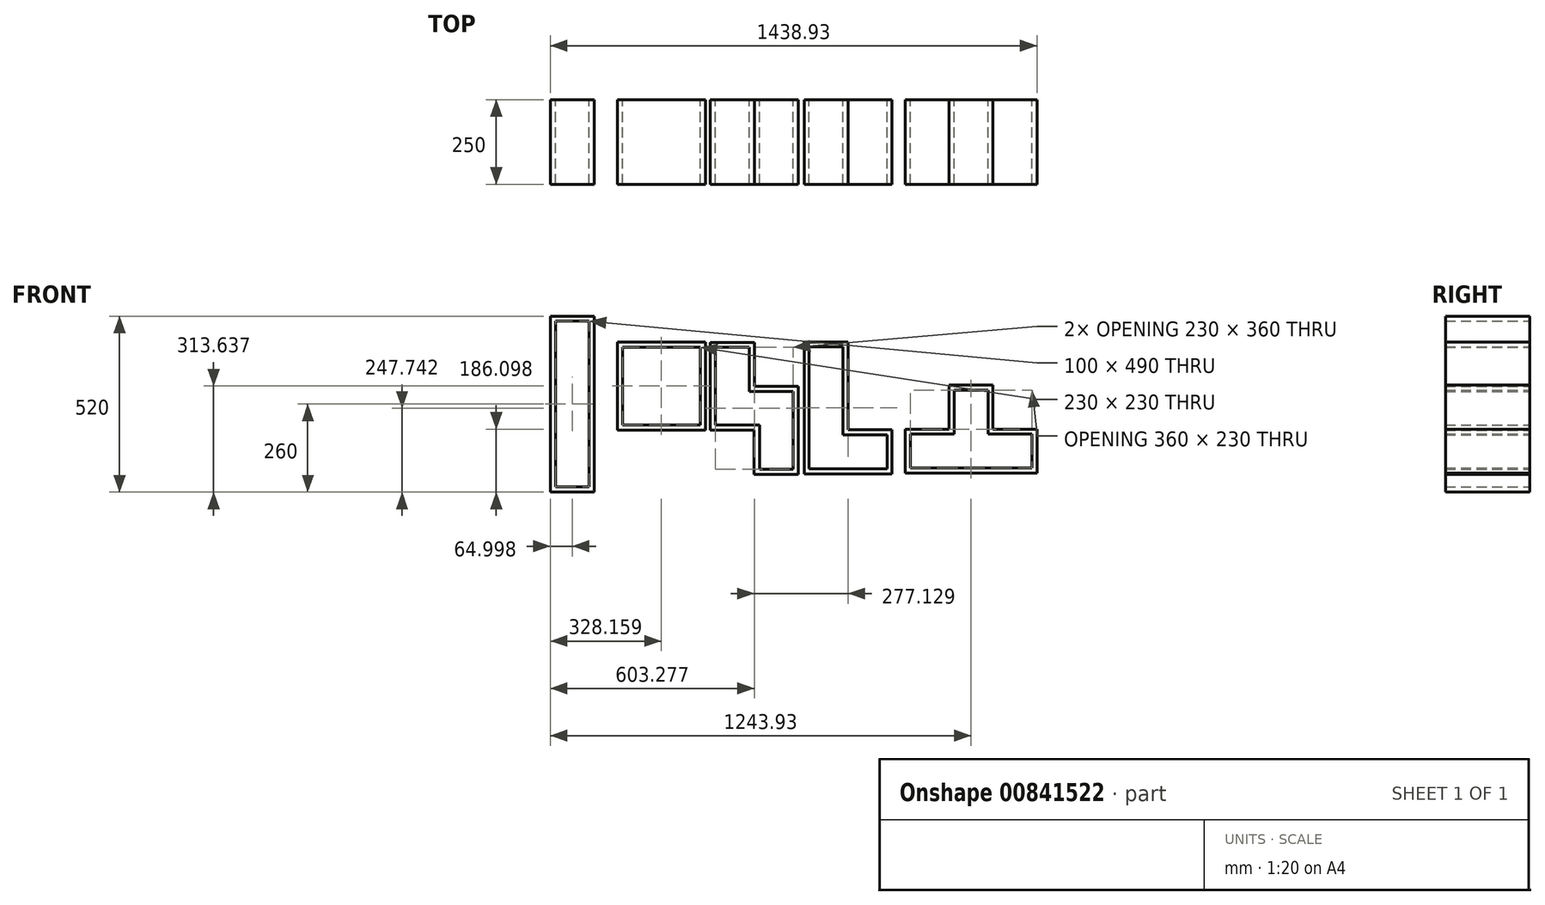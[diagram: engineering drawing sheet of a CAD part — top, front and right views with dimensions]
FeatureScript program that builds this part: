
annotation { "Feature Type Name" : "Feature", "Feature Type Description" : "" }
export const myFeature = defineFeature(function(context is Context, id is Id, definition is map)
    precondition{}
    {
        {
            var Q0;
            Q0=qCreatedBy(makeId("Front.planeOp"),FACE);
            var sketch = newSketch(context, id + "F0", { "sketchPlane" : qUnion([Q0])});
            skLineSegment(sketch, "E0", {"start": v(-196, 207.37) * mm, "end": v(-66, 207.37) * mm});
            skLineSegment(sketch, "E1", {"start": v(-66, 207.37) * mm, "end": v(-66, 77.37) * mm});
            skLineSegment(sketch, "E2", {"start": v(-66, 77.37) * mm, "end": v(64, 77.37) * mm});
            skLineSegment(sketch, "E3", {"start": v(64, 77.37) * mm, "end": v(64, -182.63) * mm});
            skLineSegment(sketch, "E4", {"start": v(64, -182.63) * mm, "end": v(-67, -182.63) * mm});
            skLineSegment(sketch, "E5", {"start": v(-67, -182.63) * mm, "end": v(-67, -52.63) * mm});
            skLineSegment(sketch, "E6", {"start": v(-196, -52.63) * mm, "end": v(-196, 207.37) * mm});
            skLineSegment(sketch, "E7", {"start": v(-196, -52.63) * mm, "end": v(-67, -52.63) * mm});
            skLineSegment(sketch, "E8", {"start": v(-181, 192.37) * mm, "end": v(-181, -37.63) * mm});
            skLineSegment(sketch, "E9", {"start": v(-181, -37.63) * mm, "end": v(-51, -37.63) * mm});
            skLineSegment(sketch, "E10", {"start": v(-51, -37.63) * mm, "end": v(-51, -167.63) * mm});
            skLineSegment(sketch, "E11", {"start": v(-51, -167.63) * mm, "end": v(49, -167.63) * mm});
            skLineSegment(sketch, "E12", {"start": v(49, -167.63) * mm, "end": v(49, 62.37) * mm});
            skLineSegment(sketch, "E13", {"start": v(49, 62.37) * mm, "end": v(-81, 62.37) * mm});
            skLineSegment(sketch, "E14", {"start": v(-81, 62.37) * mm, "end": v(-81, 192.37) * mm});
            skLineSegment(sketch, "E15", {"start": v(-81, 192.37) * mm, "end": v(-181, 192.37) * mm});
            skLineSegment(sketch, "E16", {"start": v(-196, 175.02) * mm, "end": v(-181, 175.02) * mm, "construction": true});
            skLineSegment(sketch, "E17", {"start": v(-131, 207.37) * mm, "end": v(-131, 192.37) * mm, "construction": true});
            skLineSegment(sketch, "E18", {"start": v(-3.9, 77.37) * mm, "end": v(-3.9, 62.37) * mm, "construction": true});
            skLineSegment(sketch, "E19", {"start": v(49, -86.83) * mm, "end": v(64, -86.83) * mm, "construction": true});
            skLineSegment(sketch, "E20", {"start": v(10.57, -167.63) * mm, "end": v(10.57, -182.63) * mm, "construction": true});
            skLineSegment(sketch, "E21", {"start": v(-144.39, -37.63) * mm, "end": v(-144.39, -52.63) * mm, "construction": true});
            skSolve(sketch);
        }
        {
            var Q0;
            Q0=qCreatedBy(makeId("Front.planeOp"),FACE);
            var sketch = newSketch(context, id + "F1", { "sketchPlane" : qUnion([Q0])});
            skLineSegment(sketch, "E22.bottom", {"start": v(-471.11, 208.27) * mm, "end": v(-211.11, 208.27) * mm});
            skLineSegment(sketch, "E22.top", {"start": v(-471.11, -51.73) * mm, "end": v(-211.11, -51.73) * mm});
            skLineSegment(sketch, "E22.left", {"start": v(-471.11, 208.27) * mm, "end": v(-471.11, -51.73) * mm});
            skLineSegment(sketch, "E22.right", {"start": v(-211.11, 208.27) * mm, "end": v(-211.11, -51.73) * mm});
            skLineSegment(sketch, "E23.bottom", {"start": v(-456.11, 193.27) * mm, "end": v(-226.11, 193.27) * mm});
            skLineSegment(sketch, "E23.top", {"start": v(-456.11, -36.73) * mm, "end": v(-226.11, -36.73) * mm});
            skLineSegment(sketch, "E23.left", {"start": v(-456.11, 193.27) * mm, "end": v(-456.11, -36.73) * mm});
            skLineSegment(sketch, "E23.right", {"start": v(-226.11, 193.27) * mm, "end": v(-226.11, -36.73) * mm});
            skLineSegment(sketch, "E24", {"start": v(-471.11, 102.95) * mm, "end": v(-456.11, 102.95) * mm, "construction": true});
            skLineSegment(sketch, "E25", {"start": v(-393.58, -36.73) * mm, "end": v(-393.58, -51.73) * mm, "construction": true});
            skSolve(sketch);
        }
        {
            var Q0;
            Q0=qCreatedBy(makeId("Front.planeOp"),FACE);
            var sketch = newSketch(context, id + "F2", { "sketchPlane" : qUnion([Q0])});
            skLineSegment(sketch, "E26", {"start": v(81.14, 208.65) * mm, "end": v(81.14, -181.35) * mm});
            skLineSegment(sketch, "E27", {"start": v(81.14, -181.35) * mm, "end": v(341.14, -181.35) * mm});
            skLineSegment(sketch, "E28", {"start": v(341.14, -181.35) * mm, "end": v(341.14, -51.35) * mm});
            skLineSegment(sketch, "E29", {"start": v(341.14, -51.35) * mm, "end": v(211.14, -51.35) * mm});
            skLineSegment(sketch, "E30", {"start": v(211.14, -51.35) * mm, "end": v(211.14, 208.65) * mm});
            skLineSegment(sketch, "E31", {"start": v(211.14, 208.65) * mm, "end": v(81.14, 208.65) * mm});
            skLineSegment(sketch, "E32", {"start": v(96.14, 193.65) * mm, "end": v(96.14, -166.35) * mm});
            skLineSegment(sketch, "E33", {"start": v(96.14, -166.35) * mm, "end": v(326.14, -166.35) * mm});
            skLineSegment(sketch, "E34", {"start": v(326.14, -166.35) * mm, "end": v(326.14, -66.35) * mm});
            skLineSegment(sketch, "E35", {"start": v(326.14, -66.35) * mm, "end": v(196.14, -66.35) * mm});
            skLineSegment(sketch, "E36", {"start": v(196.14, -66.35) * mm, "end": v(196.14, 193.65) * mm});
            skLineSegment(sketch, "E37", {"start": v(196.14, 193.65) * mm, "end": v(96.14, 193.65) * mm});
            skLineSegment(sketch, "E38", {"start": v(81.14, 13.65) * mm, "end": v(96.14, 13.65) * mm, "construction": true});
            skLineSegment(sketch, "E39", {"start": v(196.14, 41.47) * mm, "end": v(211.14, 41.47) * mm, "construction": true});
            skLineSegment(sketch, "E40", {"start": v(248.46, -166.35) * mm, "end": v(248.46, -181.35) * mm, "construction": true});
            skPoint(sketch, "E41.startSnap0", {"position": v(341.14, -116.35) * mm});
            skLineSegment(sketch, "E42", {"start": v(160.63, 208.65) * mm, "end": v(160.63, 193.65) * mm, "construction": true});
            skLineSegment(sketch, "E43", {"start": v(326.14, -66.35) * mm, "end": v(326.14, -51.35) * mm, "construction": true});
            skLineSegment(sketch, "E44", {"start": v(326.14, -66.35) * mm, "end": v(341.14, -66.35) * mm, "construction": true});
            skSolve(sketch);
        }
        {
            var Q0;
            Q0=qCreatedBy(makeId("Front.planeOp"),FACE);
            var sketch = newSketch(context, id + "F3", { "sketchPlane" : qUnion([Q0])});
            skLineSegment(sketch, "E45.bottom", {"start": v(-669.27, 284.63) * mm, "end": v(-539.27, 284.63) * mm});
            skLineSegment(sketch, "E45.top", {"start": v(-669.27, -235.37) * mm, "end": v(-539.27, -235.37) * mm});
            skLineSegment(sketch, "E45.left", {"start": v(-669.27, 284.63) * mm, "end": v(-669.27, -235.37) * mm});
            skLineSegment(sketch, "E45.right", {"start": v(-539.27, 284.63) * mm, "end": v(-539.27, -235.37) * mm});
            skLineSegment(sketch, "E46.bottom", {"start": v(-654.27, 269.63) * mm, "end": v(-554.27, 269.63) * mm});
            skLineSegment(sketch, "E46.top", {"start": v(-654.27, -220.37) * mm, "end": v(-554.27, -220.37) * mm});
            skLineSegment(sketch, "E46.left", {"start": v(-654.27, 269.63) * mm, "end": v(-654.27, -220.37) * mm});
            skLineSegment(sketch, "E46.right", {"start": v(-554.27, 269.63) * mm, "end": v(-554.27, -220.37) * mm});
            skLineSegment(sketch, "E47", {"start": v(-604.27, 269.63) * mm, "end": v(-604.27, 284.63) * mm, "construction": true});
            skLineSegment(sketch, "E48", {"start": v(-595.97, -220.37) * mm, "end": v(-595.97, -235.37) * mm, "construction": true});
            skLineSegment(sketch, "E49", {"start": v(-669.27, 39.86) * mm, "end": v(-654.27, 39.86) * mm, "construction": true});
            skSolve(sketch);
        }
        {
            var Q0;
            Q0=qCreatedBy(makeId("Front.planeOp"),FACE);
            var sketch = newSketch(context, id + "F4", { "sketchPlane" : qUnion([Q0])});
            skLineSegment(sketch, "E50", {"start": v(379.66, -49.27) * mm, "end": v(379.66, -179.27) * mm});
            skLineSegment(sketch, "E51", {"start": v(379.66, -179.27) * mm, "end": v(769.66, -179.27) * mm});
            skLineSegment(sketch, "E52", {"start": v(769.66, -179.27) * mm, "end": v(769.66, -49.27) * mm});
            skLineSegment(sketch, "E53", {"start": v(769.66, -49.27) * mm, "end": v(639.66, -49.27) * mm});
            skLineSegment(sketch, "E54", {"start": v(639.66, -49.27) * mm, "end": v(639.66, 80.73) * mm});
            skLineSegment(sketch, "E55", {"start": v(639.66, 80.73) * mm, "end": v(509.66, 80.73) * mm});
            skLineSegment(sketch, "E56", {"start": v(509.66, 80.73) * mm, "end": v(509.66, -49.27) * mm});
            skLineSegment(sketch, "E57", {"start": v(509.66, -49.27) * mm, "end": v(379.66, -49.27) * mm});
            skLineSegment(sketch, "E58", {"start": v(524.66, 65.73) * mm, "end": v(524.66, -64.27) * mm});
            skLineSegment(sketch, "E59", {"start": v(524.66, -64.27) * mm, "end": v(394.66, -64.27) * mm});
            skLineSegment(sketch, "E60", {"start": v(394.66, -64.27) * mm, "end": v(394.66, -164.27) * mm});
            skLineSegment(sketch, "E61", {"start": v(394.66, -164.27) * mm, "end": v(754.66, -164.27) * mm});
            skLineSegment(sketch, "E62", {"start": v(754.66, -164.27) * mm, "end": v(754.66, -64.27) * mm});
            skLineSegment(sketch, "E63", {"start": v(754.66, -64.27) * mm, "end": v(624.66, -64.27) * mm});
            skLineSegment(sketch, "E64", {"start": v(624.66, -64.27) * mm, "end": v(624.66, 65.73) * mm});
            skLineSegment(sketch, "E65", {"start": v(624.66, 65.73) * mm, "end": v(524.66, 65.73) * mm});
            skLineSegment(sketch, "E66", {"start": v(394.66, -114.27) * mm, "end": v(379.66, -114.27) * mm, "construction": true});
            skLineSegment(sketch, "E67", {"start": v(600.89, -164.27) * mm, "end": v(600.89, -179.27) * mm, "construction": true});
            skLineSegment(sketch, "E68", {"start": v(598.83, 65.73) * mm, "end": v(598.83, 80.73) * mm, "construction": true});
            skLineSegment(sketch, "E69", {"start": v(509.66, 32.73) * mm, "end": v(524.66, 32.73) * mm, "construction": true});
            skSolve(sketch);
        }
        {
            var Q0;
            {var subQ4=sQuery(id+"F2.wireOp",EDGE,"E29");Q0=makeQuery(id+"F2.imprint","IMPRINT",FACE,{"disambiguationData":[TD([[makeQuery(id+"F2.imprint","IMPRINT",EDGE,{"derivedFrom":subQ4}),1.0]])]});}
            extrude(context, id + "F5", {"entities" : qUnion([Q0]), "depth" : 250 * mm, "offsetDistance" : 25 * mm});
        }
        {
            var Q0;
            Q0=makeQuery(id+"F4.imprint","IMPRINT",FACE,{"disambiguationData":[TD([[makeQuery(id+"F4.imprint","IMPRINT",EDGE,{"derivedFrom":sQuery(id+"F4.wireOp",EDGE,"E50")}),1.0]])]});
            extrude(context, id + "F6", {"entities" : qUnion([Q0]), "depth" : 250 * mm, "offsetDistance" : 25 * mm});
        }
        {
            var Q0;
            Q0=makeQuery(id+"F0.imprint","IMPRINT",FACE,{"disambiguationData":[TD([[makeQuery(id+"F0.imprint","IMPRINT",EDGE,{"derivedFrom":sQuery(id+"F0.wireOp",EDGE,"E0")}),-1.0]])]});
            extrude(context, id + "F7", {"entities" : qUnion([Q0]), "depth" : 250 * mm, "offsetDistance" : 25 * mm});
        }
        {
            var Q0;
            Q0=makeQuery(id+"F3.imprint","IMPRINT",FACE,{"disambiguationData":[TD([[makeQuery(id+"F3.imprint","IMPRINT",EDGE,{"derivedFrom":sQuery(id+"F3.wireOp",EDGE,"E45.bottom")}),-1.0]])]});
            extrude(context, id + "F8", {"entities" : qUnion([Q0]), "depth" : 250 * mm, "offsetDistance" : 25 * mm});
        }
        {
            var Q0;
            Q0=makeQuery(id+"F1.imprint","IMPRINT",FACE,{"disambiguationData":[TD([[makeQuery(id+"F1.imprint","IMPRINT",EDGE,{"derivedFrom":sQuery(id+"F1.wireOp",EDGE,"E22.bottom")}),-1.0]])]});
            extrude(context, id + "F9", {"entities" : qUnion([Q0]), "depth" : 250 * mm, "offsetDistance" : 25 * mm});
        }
    });
